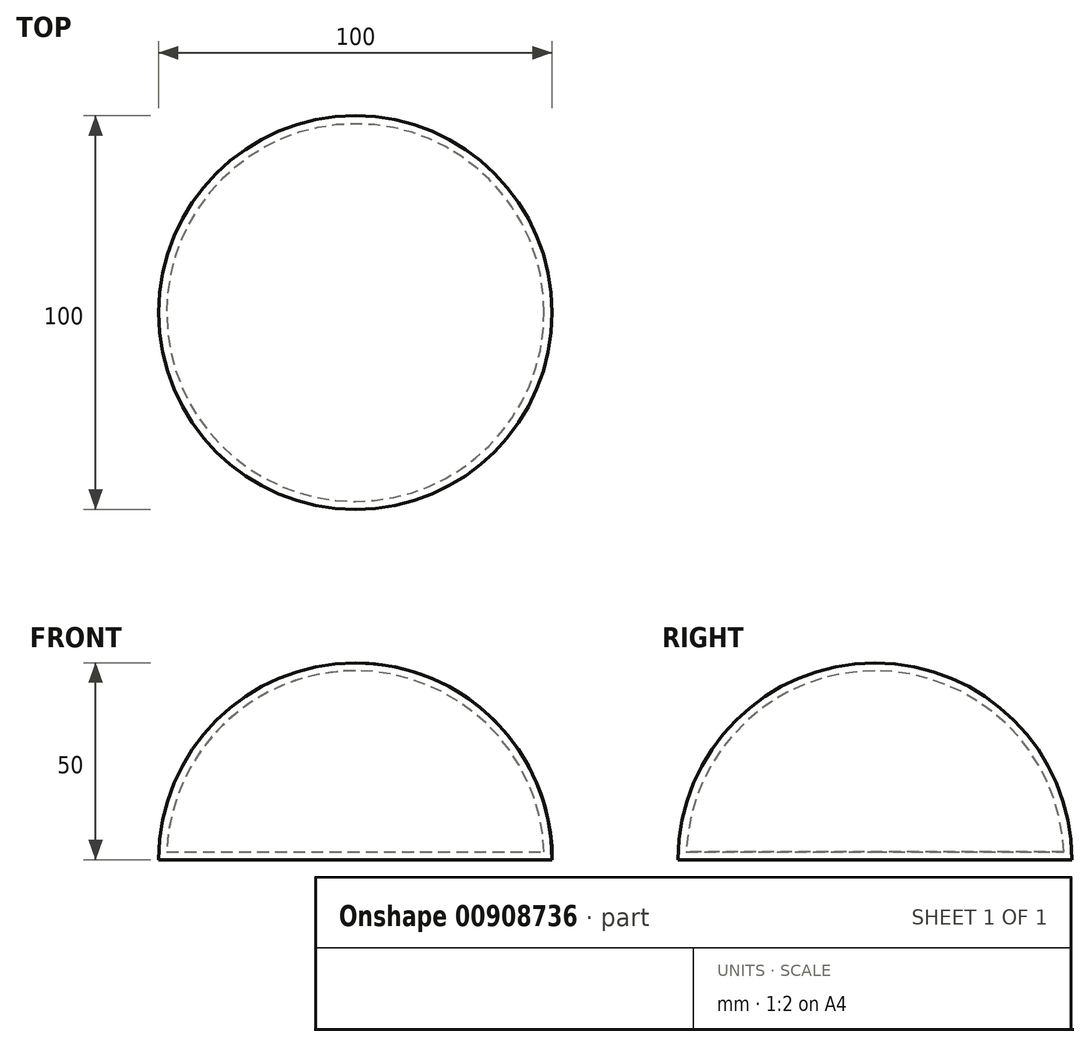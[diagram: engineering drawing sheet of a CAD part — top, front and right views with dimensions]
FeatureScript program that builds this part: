
annotation { "Feature Type Name" : "Feature", "Feature Type Description" : "" }
export const myFeature = defineFeature(function(context is Context, id is Id, definition is map)
    precondition{}
    {
        {
            var Q0;
            Q0=qCreatedBy(makeId("Front.planeOp"),FACE);
            var sketch = newSketch(context, id + "F0", { "sketchPlane" : qUnion([Q0])});
            skArc(sketch, "E0", {"start": v(0, 50) * mm, "mid": v(-35.36, 35.36) * mm, "end": v(-50, 0) * mm});
            skArc(sketch, "E1", {"start": v(0, 48) * mm, "mid": v(-33.23, 34.64) * mm, "end": v(-47.96, 2) * mm});
            skLineSegment(sketch, "E2", {"start": v(0, 0) * mm, "end": v(-66.05, 0) * mm});
            skLineSegment(sketch, "E3", {"start": v(0, 0) * mm, "end": v(0, 63.65) * mm});
            skLineSegment(sketch, "E4", {"start": v(0, 2) * mm, "end": v(-47.96, 2) * mm});
            skSolve(sketch);
        }
        {
            var Q0;
            {var subQ4=sQuery(id+"F0.wireOp",EDGE,"E0");Q0=makeQuery(id+"F0.imprint","IMPRINT",FACE,{"disambiguationData":[TD([[makeQuery(id+"F0.imprint","IMPRINT",EDGE,{"derivedFrom":subQ4}),1.0]])]});}
            var Q1;
            Q1=sQuery(id+"F0.wireOp",EDGE,"E3");
            revolve(context, id + "F1", {"surfaceOperationType" : NewSurfaceOperationType.NEW, "entities" : qUnion([Q0]), "axis" : qUnion([Q1]), "revolveType" : RevolveType.FULL});
        }
    });
